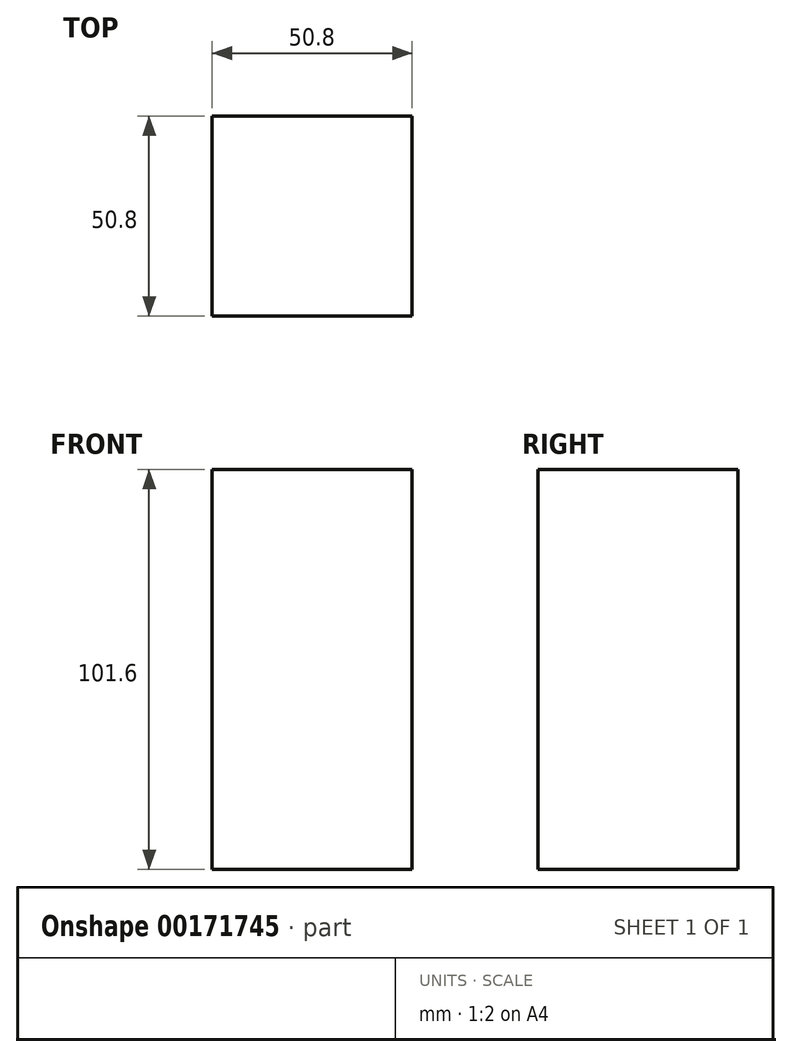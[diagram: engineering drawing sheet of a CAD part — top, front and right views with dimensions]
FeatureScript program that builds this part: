
annotation { "Feature Type Name" : "Feature", "Feature Type Description" : "" }
export const myFeature = defineFeature(function(context is Context, id is Id, definition is map)
    precondition{}
    {
        {
            var Q0;
            Q0=qCreatedBy(makeId("Top.planeOp"),FACE);
            var sketch = newSketch(context, id + "F0", { "sketchPlane" : qUnion([Q0])});
            skLineSegment(sketch, "E0.bottom", {"start": v(0, 0) * mm, "end": v(50.8, 0) * mm});
            skLineSegment(sketch, "E0.top", {"start": v(0, -50.8) * mm, "end": v(50.8, -50.8) * mm});
            skLineSegment(sketch, "E0.left", {"start": v(0, 0) * mm, "end": v(0, -50.8) * mm});
            skLineSegment(sketch, "E0.right", {"start": v(50.8, 0) * mm, "end": v(50.8, -50.8) * mm});
            skSolve(sketch);
        }
        {
            var Q0;
            Q0 = qSketchRegion(id + "F0", true);
            extrude(context, id + "F1", {"entities" : qUnion([Q0]), "depth" : 101.6 * mm});
        }
    });
